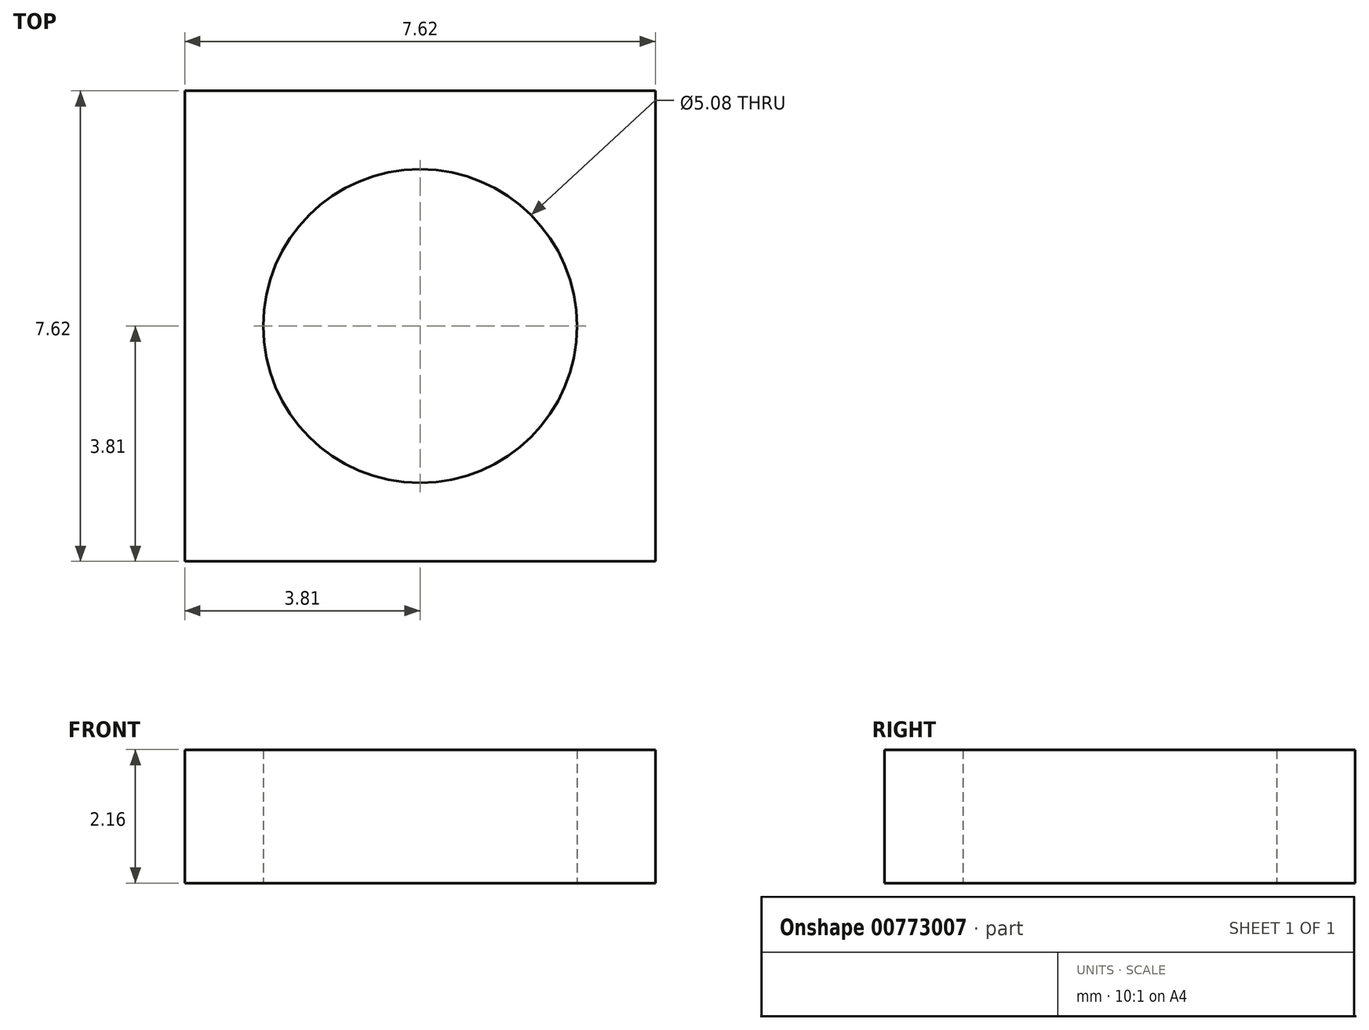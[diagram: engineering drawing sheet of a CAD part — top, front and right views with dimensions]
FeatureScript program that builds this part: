
annotation { "Feature Type Name" : "Feature", "Feature Type Description" : "" }
export const myFeature = defineFeature(function(context is Context, id is Id, definition is map)
    precondition{}
    {
        {
            var Q0;
            Q0=qCreatedBy(makeId("Top.planeOp"),FACE);
            var sketch = newSketch(context, id + "F0", { "sketchPlane" : qUnion([Q0])});
            skLineSegment(sketch, "E0.bottom", {"start": v(0, 0) * mm, "end": v(-3.81, 0) * mm});
            skLineSegment(sketch, "E0.top", {"start": v(0, 7.62) * mm, "end": v(-3.81, 7.62) * mm});
            skLineSegment(sketch, "E0.left", {"start": v(0, 0) * mm, "end": v(0, 7.62) * mm});
            skLineSegment(sketch, "E0.right", {"start": v(-3.8, 0) * mm, "end": v(-3.81, 7.62) * mm});
            skLineSegment(sketch, "E1.MirrorCS", {"start": v(0, 7.62) * mm, "end": v(3.81, 7.62) * mm});
            skLineSegment(sketch, "E2.MirrorCS", {"start": v(3.8, 0) * mm, "end": v(3.81, 7.62) * mm});
            skLineSegment(sketch, "E3.MirrorCS", {"start": v(0, 0) * mm, "end": v(3.81, 0) * mm});
            skLineSegment(sketch, "E4", {"start": v(0, 7.62) * mm, "end": v(0, 3.81) * mm});
            skCircle(sketch, "E5", {"center": v(0, 3.81) * mm, "radius": 2.54 * mm});
            skSolve(sketch);
        }
        {
            var Q0;
            Q0 = qSketchRegion(id + "F0", true);
            extrude(context, id + "F1", {"entities" : qUnion([Q0]), "depth" : 2.16 * mm, "offsetDistance" : 25.4 * mm});
        }
    });
